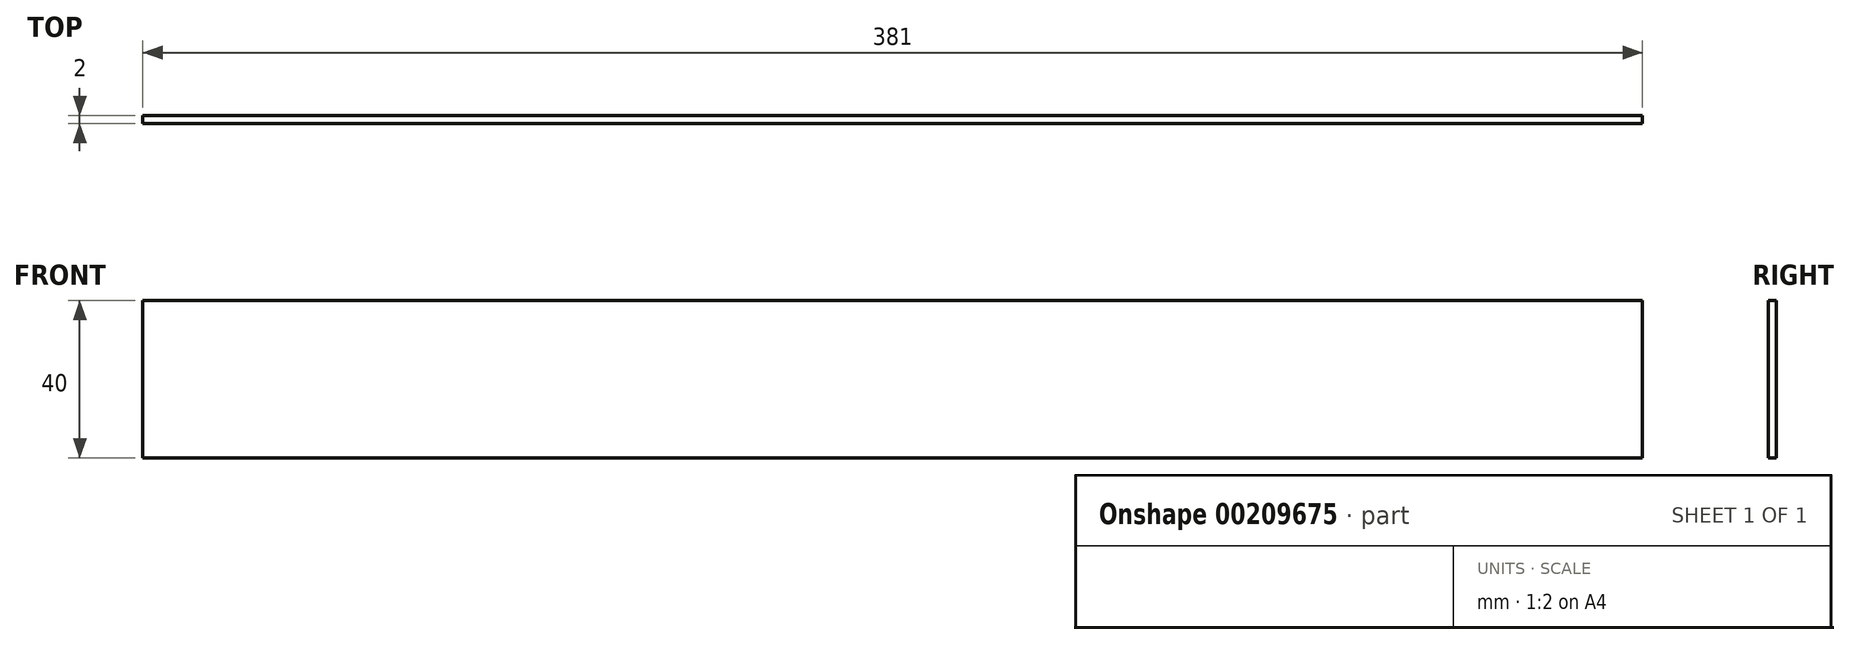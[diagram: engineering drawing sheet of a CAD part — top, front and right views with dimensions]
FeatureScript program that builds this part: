
annotation { "Feature Type Name" : "Feature", "Feature Type Description" : "" }
export const myFeature = defineFeature(function(context is Context, id is Id, definition is map)
    precondition{}
    {
        {
            var Q0;
            Q0=qCreatedBy(makeId("Front.planeOp"),FACE);
            var sketch = newSketch(context, id + "F0", { "sketchPlane" : qUnion([Q0])});
            skLineSegment(sketch, "E0.bottom", {"start": v(168.65, -10.73) * mm, "end": v(-212.35, -10.73) * mm});
            skLineSegment(sketch, "E0.top", {"start": v(168.65, 29.27) * mm, "end": v(-212.35, 29.27) * mm});
            skLineSegment(sketch, "E0.left", {"start": v(168.65, -10.73) * mm, "end": v(168.65, 29.27) * mm});
            skLineSegment(sketch, "E0.right", {"start": v(-212.35, -10.73) * mm, "end": v(-212.35, 29.27) * mm});
            skPoint(sketch, "E0.middle", {"position": v(-21.85, 9.27) * mm});
            skSolve(sketch);
        }
        {
            var Q0;
            Q0=makeQuery(id+"F0.imprint","IMPRINT",FACE,{"disambiguationData":[TD([[makeQuery(id+"F0.imprint","IMPRINT",EDGE,{"derivedFrom":sQuery(id+"F0.wireOp",EDGE,"E0.bottom")}),-1.0]])]});
            extrude(context, id + "F1", {"entities" : qUnion([Q0]), "depth" : 2 * mm});
        }
    });
